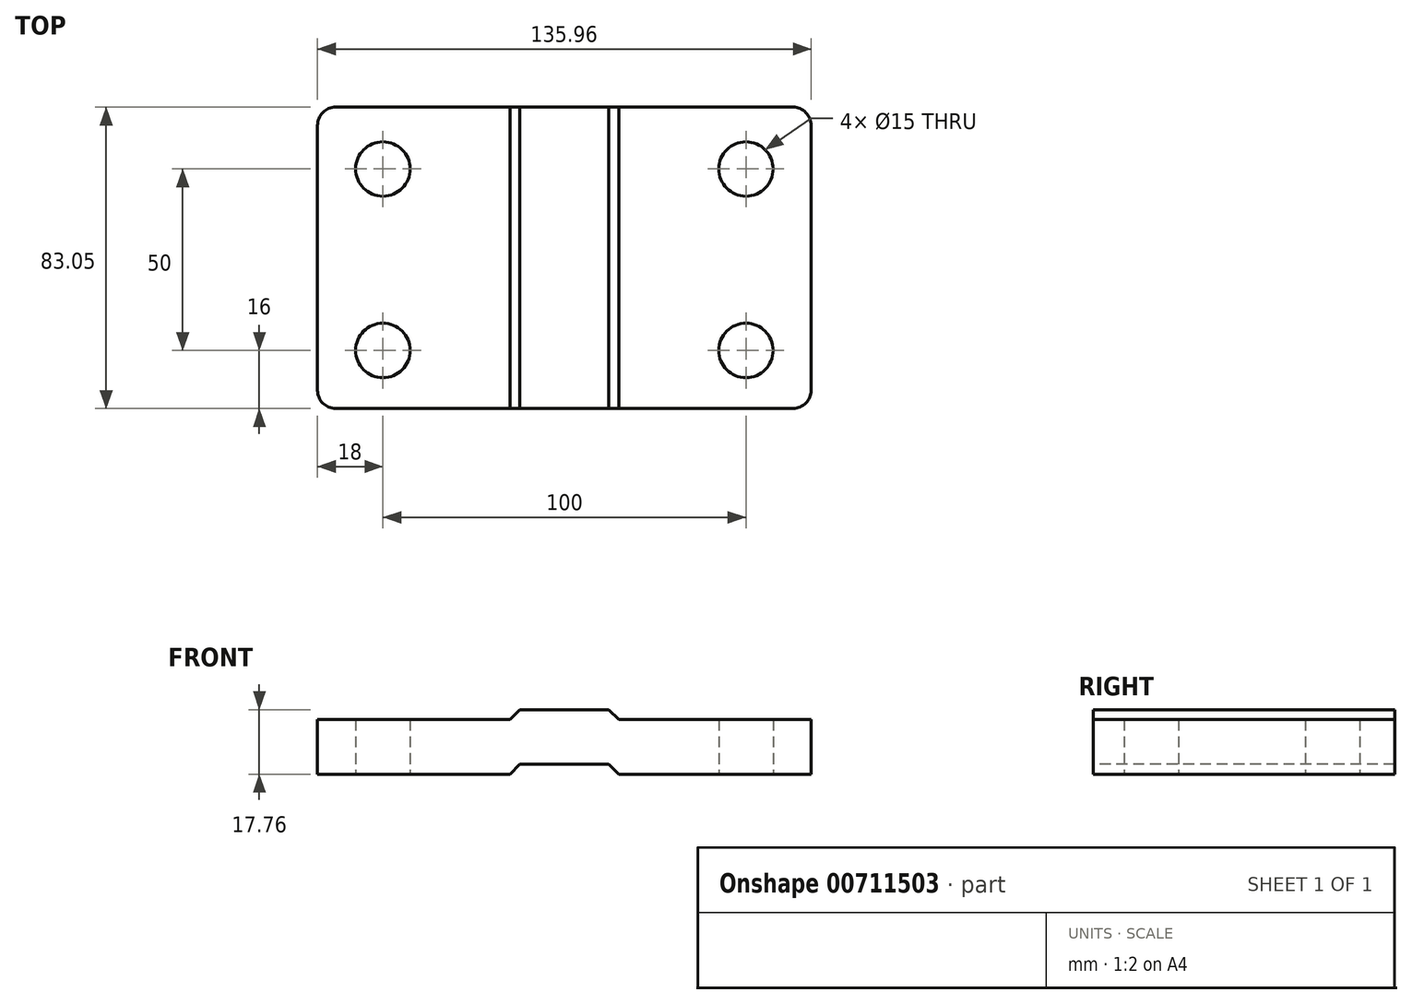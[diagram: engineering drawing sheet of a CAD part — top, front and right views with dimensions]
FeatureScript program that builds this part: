
annotation { "Feature Type Name" : "Feature", "Feature Type Description" : "" }
export const myFeature = defineFeature(function(context is Context, id is Id, definition is map)
    precondition{}
    {
        {
            var Q0;
            Q0=qCreatedBy(makeId("Top.planeOp"),FACE);
            var sketch = newSketch(context, id + "F0", { "sketchPlane" : qUnion([Q0])});
            skLineSegment(sketch, "E0", {"start": v(0, 0) * mm, "end": v(-67.98, 0) * mm});
            skLineSegment(sketch, "E1.MirrorCS", {"start": v(0, 0) * mm, "end": v(67.98, 0) * mm});
            skLineSegment(sketch, "E2", {"start": v(-67.98, 0) * mm, "end": v(-67.98, 83.05) * mm});
            skLineSegment(sketch, "E3", {"start": v(-67.98, 83.05) * mm, "end": v(67.98, 83.05) * mm});
            skLineSegment(sketch, "E4", {"start": v(67.98, 83.05) * mm, "end": v(67.98, 0) * mm});
            skSolve(sketch);
        }
        {
            var Q0;
            Q0=makeQuery(id+"F0.imprint","IMPRINT",FACE,{"disambiguationData":[TD([[makeQuery(id+"F0.imprint","IMPRINT",EDGE,{"derivedFrom":sQuery(id+"F0.wireOp",EDGE,"E0")}),-1.0]])]});
            extrude(context, id + "F1", {"entities" : qUnion([Q0]), "depth" : 15 * mm, "offsetDistance" : 25 * mm});
        }
        {
            var Q0;
            Q0=makeQuery(id+"F1.opExtrude","SWEPT_FACE",FACE,{"disambiguationData":[OSD([sQuery(id+"F0.wireOp",EDGE,"E0"),sQuery(id+"F0.wireOp",EDGE,"E1.MirrorCS")])]});
            cPlane(context, id + "F2", {"entities" : qUnion([Q0]), "cplaneType" : CPlaneType.OFFSET, "offset" : 0 * mm, "width" : 150 * mm, "height" : 150 * mm});
        }
        {
            var Q0;
            Q0=qCreatedBy(id+"F2.planeOp",FACE);
            var sketch = newSketch(context, id + "F3", { "sketchPlane" : qUnion([Q0])});
            skLineSegment(sketch, "E5", {"start": v(0, 0) * mm, "end": v(-15, 0) * mm});
            skLineSegment(sketch, "E6.MirrorCS", {"start": v(0, 0) * mm, "end": v(15, 0) * mm});
            skLineSegment(sketch, "E7", {"start": v(-12.24, 2.76) * mm, "end": v(12.24, 2.76) * mm});
            skLineSegment(sketch, "E8", {"start": v(-15, 0) * mm, "end": v(-12.24, 2.76) * mm});
            skLineSegment(sketch, "E9", {"start": v(15, 0) * mm, "end": v(12.24, 2.76) * mm});
            skSolve(sketch);
        }
        {
            var Q0;
            Q0=makeQuery(id+"F3.imprint","IMPRINT",FACE,{"disambiguationData":[TD([[makeQuery(id+"F3.imprint","IMPRINT",EDGE,{"derivedFrom":sQuery(id+"F3.wireOp",EDGE,"E5")}),-1.0]])]});
            extrude(context, id + "F4", {"entities" : qUnion([Q0]), "operationType" : NewBodyOperationType.REMOVE, "endBound" : BoundingType.THROUGH_ALL, "oppositeDirection" : true, "depth" : 25 * mm, "offsetDistance" : 25 * mm});
        }
        {
            var Q0;
            Q0=qCreatedBy(id+"F2.planeOp",FACE);
            cPlane(context, id + "F5", {"entities" : qUnion([Q0]), "cplaneType" : CPlaneType.OFFSET, "offset" : 0 * mm, "width" : 150 * mm, "height" : 150 * mm});
        }
        {
            var Q0;
            Q0=qCreatedBy(id+"F5.planeOp",FACE);
            var sketch = newSketch(context, id + "F6", { "sketchPlane" : qUnion([Q0])});
            skPoint(sketch, "E10", {"position": v(0, 15) * mm});
            skLineSegment(sketch, "E11", {"start": v(0, 15) * mm, "end": v(-15, 15) * mm});
            skLineSegment(sketch, "E12.MirrorCS", {"start": v(0, 15) * mm, "end": v(15, 15) * mm});
            skLineSegment(sketch, "E13", {"start": v(-12.24, 17.76) * mm, "end": v(12.24, 17.76) * mm});
            skLineSegment(sketch, "E14", {"start": v(-15, 15) * mm, "end": v(-12.24, 17.76) * mm});
            skLineSegment(sketch, "E15", {"start": v(15, 15) * mm, "end": v(12.24, 17.76) * mm});
            skSolve(sketch);
        }
        {
            var Q0;
            Q0=makeQuery(id+"F6.imprint","IMPRINT",FACE,{"disambiguationData":[TD([[makeQuery(id+"F6.imprint","IMPRINT",EDGE,{"derivedFrom":sQuery(id+"F6.wireOp",EDGE,"E11")}),-1.0]])]});
            extrude(context, id + "F7", {"entities" : qUnion([Q0]), "operationType" : NewBodyOperationType.ADD, "oppositeDirection" : true, "depth" : 83.05 * mm, "offsetDistance" : 25 * mm});
        }
        {
            var Q0;
            Q0=makeQuery(id+"F1.opExtrude","SWEPT_EDGE",EDGE,{"disambiguationData":[OSD([sQuery(id+"F0.wireOp",EDGE,"E0"),sQuery(id+"F0.wireOp",EDGE,"E2")])]});
            var Q1;
            Q1=makeQuery(id+"F1.opExtrude","SWEPT_EDGE",EDGE,{"disambiguationData":[OSD([sQuery(id+"F0.wireOp",EDGE,"E1.MirrorCS"),sQuery(id+"F0.wireOp",EDGE,"E4")])]});
            var Q2;
            Q2=makeQuery(id+"F1.opExtrude","SWEPT_EDGE",EDGE,{"disambiguationData":[OSD([sQuery(id+"F0.wireOp",EDGE,"E3"),sQuery(id+"F0.wireOp",EDGE,"E4")])]});
            var Q3;
            Q3=makeQuery(id+"F1.opExtrude","SWEPT_EDGE",EDGE,{"disambiguationData":[OSD([sQuery(id+"F0.wireOp",EDGE,"E2"),sQuery(id+"F0.wireOp",EDGE,"E3")])]});
            fillet(context, id + "F8", {"entities" : qUnion([Q0, Q1, Q2, Q3]), "radius" : 5 * mm, "tangentPropagation" : true, "allowEdgeOverflow" : false});
        }
        {
            var Q0;
            Q0=qCreatedBy(makeId("Top.planeOp"),FACE);
            var sketch = newSketch(context, id + "F9", { "sketchPlane" : qUnion([Q0])});
            skCircle(sketch, "E16", {"center": v(-49.98, 66) * mm, "radius": 7.5 * mm});
            skCircle(sketch, "E17", {"center": v(-49.98, 16) * mm, "radius": 7.5 * mm});
            skCircle(sketch, "E18", {"center": v(50.02, 66) * mm, "radius": 7.5 * mm});
            skCircle(sketch, "E19", {"center": v(50.02, 16) * mm, "radius": 7.5 * mm});
            skSolve(sketch);
        }
        {
            var Q0;
            Q0=sQuery(id+"F9.wireOp",VERTEX,"E16.center");
            var Q1;
            Q1=sQuery(id+"F9.wireOp",VERTEX,"E17.center");
            var Q2;
            Q2=sQuery(id+"F9.wireOp",VERTEX,"E18.center");
            var Q3;
            Q3=sQuery(id+"F9.wireOp",VERTEX,"E19.center");
            var Q4;
            Q4=makeQuery(id+"F1.opExtrude","SWEPT_BODY",BODY,{"disambiguationData":[OSD([sQuery(id+"F0.wireOp",EDGE,"E0"),sQuery(id+"F0.wireOp",EDGE,"E1.MirrorCS"),sQuery(id+"F0.wireOp",EDGE,"E2"),sQuery(id+"F0.wireOp",EDGE,"E3"),sQuery(id+"F0.wireOp",EDGE,"E4")])]});
            hole(context, id + "F10", {"style" : HoleStyle.SIMPLE, "endStyle" : HoleEndStyle.THROUGH, "oppositeDirection" : true, "holeDiameter" : 15 * mm, "majorDiameter" : 5 * mm, "isTappedThrough" : true, "tappedDepth" : 12 * mm, "tapClearance" : 3, "locations" : qUnion([Q0, Q1, Q2, Q3]), "scope" : qUnion([Q4])});
        }
    });
